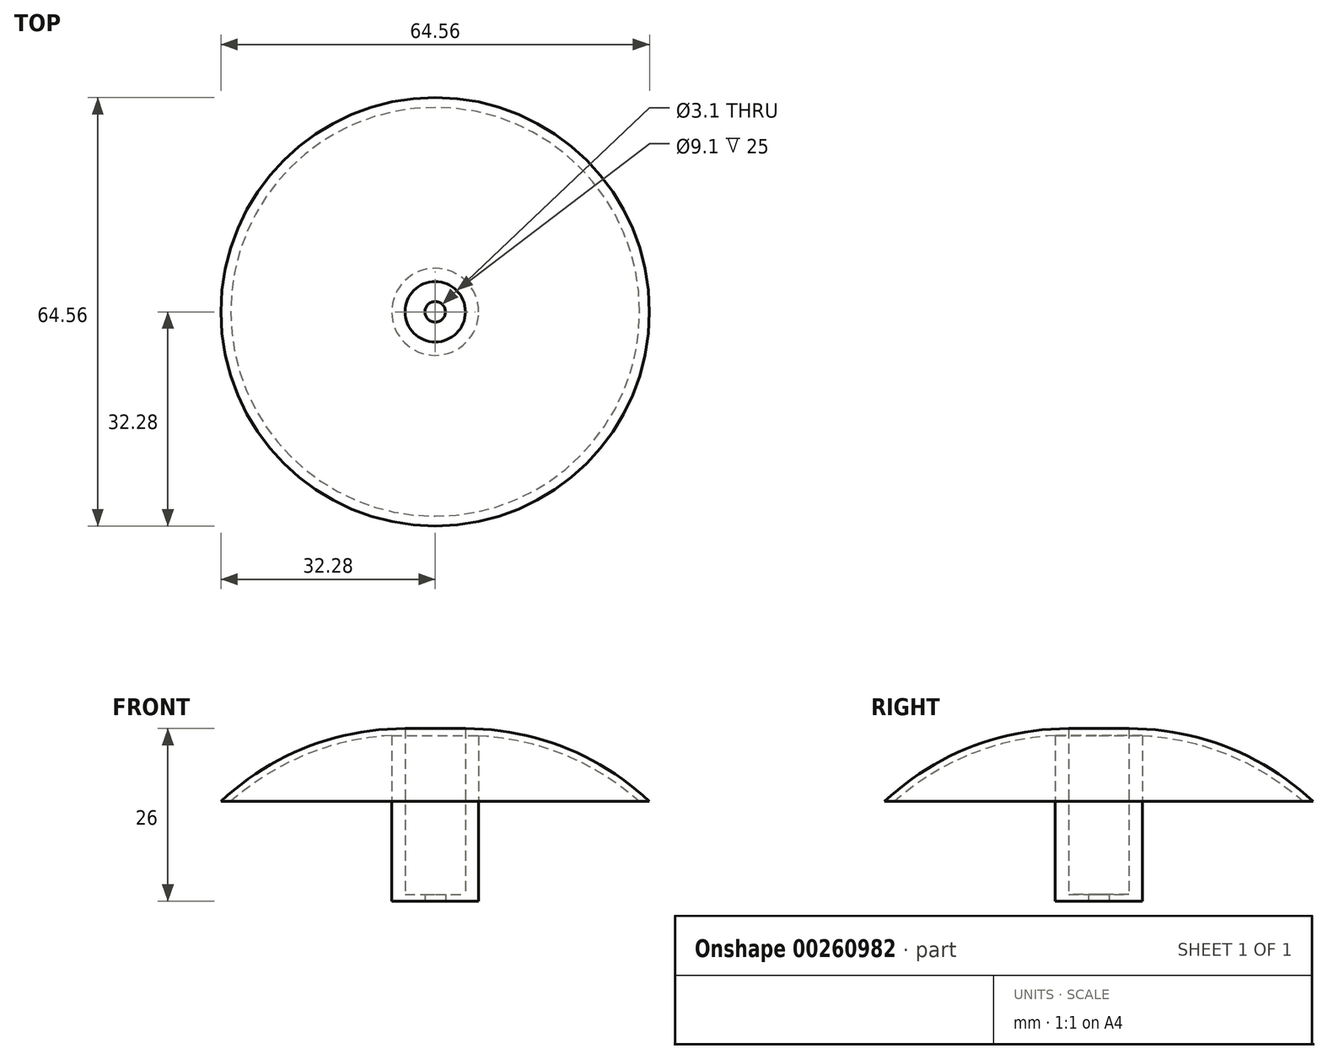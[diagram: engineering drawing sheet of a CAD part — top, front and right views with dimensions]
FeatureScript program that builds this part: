
annotation { "Feature Type Name" : "Feature", "Feature Type Description" : "" }
export const myFeature = defineFeature(function(context is Context, id is Id, definition is map)
    precondition{}
    {
        {
            var Q0;
            Q0=qCreatedBy(makeId("Front.planeOp"),FACE);
            var sketch = newSketch(context, id + "F0", { "sketchPlane" : qUnion([Q0])});
            skLineSegment(sketch, "E0", {"start": v(0, 0) * mm, "end": v(0, 27.5) * mm, "construction": true});
            skLineSegment(sketch, "E1", {"start": v(0, 0) * mm, "end": v(1.55, 0) * mm, "construction": true});
            skLineSegment(sketch, "E2", {"start": v(1.55, 0) * mm, "end": v(1.55, 2) * mm});
            skLineSegment(sketch, "E3", {"start": v(1.55, 2) * mm, "end": v(4.55, 2) * mm});
            skLineSegment(sketch, "E4", {"start": v(4.55, 2) * mm, "end": v(4.55, 17) * mm});
            skArc(sketch, "E5", {"start": v(32.28, 6) * mm, "mid": v(19.46, 14.14) * mm, "end": v(4.55, 17) * mm});
            skLineSegment(sketch, "E6", {"start": v(4.55, 17) * mm, "end": v(4.55, 15) * mm});
            skLineSegment(sketch, "E7", {"start": v(1.55, 0) * mm, "end": v(6.55, 0) * mm});
            skLineSegment(sketch, "E8", {"start": v(6.55, 0) * mm, "end": v(6.55, 14.95) * mm});
            skLineSegment(sketch, "E9", {"start": v(6.55, 0) * mm, "end": v(6.55, 6) * mm, "construction": true});
            skLineSegment(sketch, "E10", {"start": v(30.8, 6) * mm, "end": v(32.28, 6) * mm});
            skLineSegment(sketch, "E11", {"start": v(4.55, 17) * mm, "end": v(4.55, 16) * mm});
            skArc(sketch, "E12", {"start": v(30.8, 6) * mm, "mid": v(19.52, 13.04) * mm, "end": v(6.55, 15.95) * mm});
            skLineSegment(sketch, "E13", {"start": v(6.55, 14.95) * mm, "end": v(6.55, 15.95) * mm});
            skSolve(sketch);
        }
        {
            var Q0;
            Q0=makeQuery(id+"F0.imprint","IMPRINT",FACE,{"disambiguationData":[TD([[makeQuery(id+"F0.imprint","IMPRINT",EDGE,{"derivedFrom":sQuery(id+"F0.wireOp",EDGE,"E2")}),-1.0]])]});
            var Q1;
            Q1=sQuery(id+"F0.wireOp",EDGE,"E0");
            revolve(context, id + "F1", {"entities" : qUnion([Q0]), "axis" : qUnion([Q1]), "revolveType" : RevolveType.FULL});
        }
        {
            var Q0;
            Q0=makeQuery(id+"F1.opRevolve","SWEPT_FACE",FACE,{"disambiguationData":[OSD([sQuery(id+"F0.wireOp",EDGE,"E7")])]});
            extrude(context, id + "F2", {"entities" : qUnion([Q0]), "operationType" : NewBodyOperationType.ADD, "depth" : 10 * mm});
        }
        {
            var Q0;
            Q0=makeQuery(id+"F1.opRevolve","SWEPT_FACE",FACE,{"disambiguationData":[OSD([sQuery(id+"F0.wireOp",EDGE,"E3")])]});
            extrude(context, id + "F3", {"entities" : qUnion([Q0]), "operationType" : NewBodyOperationType.REMOVE, "oppositeDirection" : true, "depth" : 10 * mm});
        }
        {
            var Q0;
            Q0=makeQuery(id+"F2.opExtrude","CAP_FACE",FACE,{"disambiguationData":[OSD([sQuery(id+"F0.wireOp",EDGE,"E7")])],"isStart":false});
            extrude(context, id + "F4", {"entities" : qUnion([Q0]), "operationType" : NewBodyOperationType.REMOVE, "oppositeDirection" : true, "depth" : 1 * mm});
        }
    });
